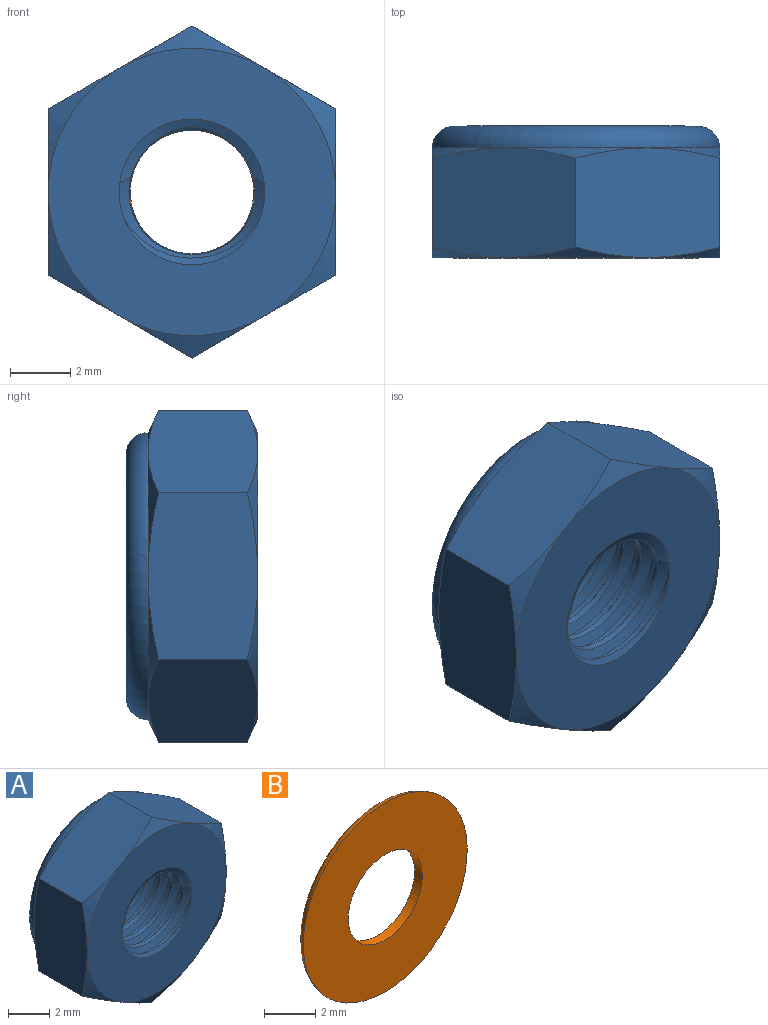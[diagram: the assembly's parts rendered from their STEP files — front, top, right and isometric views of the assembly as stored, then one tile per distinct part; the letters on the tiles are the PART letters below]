
ASSEMBLY  parts=2 mates=1
PART A: 50 faces, bbox 11.4x4.8x11.4 mm
  f0: plane 8.07x8.07mm, normal (0,1,0), area 22.1mm2, adj f1,f49
  f1: torus R=4.03mm, axis (0,-1,0), area 32.3mm2, adj f0,f2,f44,f45,f46,f47,f48
  f2: cone r=4.76mm half-angle=65deg, axis (0,-1,0), area 2.1mm2, adj f1,f3,f43
  f3: plane 5.19x4.07mm, normal (0.5,0,0.87), area 18.7mm2, adj f2,f4,f41,f42,f43,f44
  f4: cone r=5.5mm half-angle=65deg, axis (0,1,0), area 2.1mm2, adj f3,f5,f43
  f5: plane 9.53x9.53mm, normal (0,-1,0), area 53mm2, adj f4,f6,f10,f11,f12,f13,f38,f40
  f6: cone r=5.5mm half-angle=65deg, axis (0,1,0), area 2.1mm2, adj f5,f7,f43
  f7: plane 5.19x4.07mm, normal (0.5,0,-0.87), area 18.7mm2, adj f6,f8,f10,f43,f47,f48
  f8: plane 5.19x4.07mm, normal (-0.5,0,-0.87), area 18.7mm2, adj f7,f9,f10,f11,f46,f47
  f9: plane 5.94x4.07mm, normal (-1,0,0), area 18.7mm2, adj f8,f11,f12,f42,f45,f46
  f10: cone r=5.5mm half-angle=65deg, axis (0,1,0), area 2.1mm2, adj f5,f7,f8
  f11: cone r=5.5mm half-angle=65deg, axis (0,1,0), area 2.1mm2, adj f5,f8,f9
  f12: cone r=5.5mm half-angle=65deg, axis (0,1,0), area 2.1mm2, adj f5,f9,f42
  f13: cone r=2.41mm half-angle=65deg, axis (0,-1,0), area 2.3mm2, adj f5,f14,f15,f16
  f14: cone r=2.09mm half-angle=60deg, axis (0,-0.99,-0.16), area 3.1mm2, adj f13,f15,f40
  f15: cylinder r=2.09mm len=4.18mm, axis (0,0.99,0.16), area 1.8mm2, adj f13,f14,f16
  f16: cone r=2.52mm half-angle=60deg, axis (0,0.99,0.16), area 5.5mm2, adj f13,f15,f17
  f17: cylinder r=2.41mm len=4.83mm, axis (0,-1,0), area 2.9mm2, adj f16,f18
  f18: cone r=2.09mm half-angle=60deg, axis (0,-0.99,-0.16), area 5mm2, adj f17,f19
  f19: cylinder r=2.09mm len=4.18mm, axis (0,0.99,0.16), area 2.6mm2, adj f18,f20
  f20: cone r=2.52mm half-angle=60deg, axis (0,0.99,0.16), area 5.6mm2, adj f19,f21
  f21: cylinder r=2.41mm len=4.83mm, axis (0,-1,0), area 2.9mm2, adj f20,f22
  f22: cone r=2.09mm half-angle=60deg, axis (0,-0.99,-0.16), area 5mm2, adj f21,f23
  f23: cylinder r=2.09mm len=4.18mm, axis (0,0.99,0.16), area 2.6mm2, adj f22,f24
  f24: cone r=2.52mm half-angle=60deg, axis (0,0.99,0.16), area 5.6mm2, adj f23,f25
  f25: cylinder r=2.41mm len=4.83mm, axis (0,-1,0), area 2.9mm2, adj f24,f26
  f26: cone r=2.09mm half-angle=60deg, axis (0,-0.99,-0.16), area 5mm2, adj f25,f27
  f27: cylinder r=2.09mm len=4.18mm, axis (0,0.99,0.16), area 2.6mm2, adj f26,f28
  f28: cone r=2.52mm half-angle=60deg, axis (0,0.99,0.16), area 5.6mm2, adj f27,f29
  f29: cylinder r=2.41mm len=4.83mm, axis (0,-1,0), area 2.9mm2, adj f28,f30
  f30: cone r=2.09mm half-angle=60deg, axis (0,-0.99,-0.16), area 4.2mm2, adj f29,f31,f35
  f31: cylinder r=2.09mm len=4.18mm, axis (0,0.99,0.16), area 1.6mm2, adj f30,f32,f35
  f32: cone r=2.52mm half-angle=60deg, axis (0,0.99,0.16), area 2.7mm2, adj f31,f33,f34,f35
  f33: cylinder r=2.41mm len=1.1mm, axis (0,-1,0), area 0mm2, adj f32,f35
  f34: cone r=2.09mm half-angle=60deg, axis (0,-0.99,-0.16), area 0mm2, adj f32,f35
  f35: plane 9.56x9.56mm, normal (0,1,0), area 50.5mm2, adj f30,f31,f32,f33,f34,f36
  f36: torus R=4.03mm, axis (0,-1,0), area 25mm2, adj f35,f37
  f37: plane 8.07x8.07mm, normal (0,-1,0), area 22.1mm2, adj f36,f49
  f38: cone r=2.41mm half-angle=65deg, axis (0,-1,0), area 0mm2, adj f5,f39
  f39: cone r=2.52mm half-angle=60deg, axis (0,0.99,0.16), area 0mm2, adj f38,f40
  f40: cylinder r=2.41mm len=4.83mm, axis (0,-1,0), area 1.3mm2, adj f5,f14,f39
  f41: cone r=5.5mm half-angle=65deg, axis (0,1,0), area 2.1mm2, adj f3,f5,f42
  f42: plane 5.19x4.07mm, normal (-0.5,0,0.87), area 18.7mm2, adj f3,f9,f12,f41,f44,f45
  f43: plane 5.94x4.07mm, normal (1,0,0), area 18.7mm2, adj f2,f3,f4,f6,f7,f48
  f44: cone r=4.76mm half-angle=65deg, axis (0,-1,0), area 2.1mm2, adj f1,f3,f42
  f45: cone r=4.76mm half-angle=65deg, axis (0,-1,0), area 2.1mm2, adj f1,f9,f42
  f46: cone r=4.76mm half-angle=65deg, axis (0,-1,0), area 2.1mm2, adj f1,f8,f9
  f47: cone r=4.76mm half-angle=65deg, axis (0,-1,0), area 2.1mm2, adj f1,f7,f8
  f48: cone r=4.76mm half-angle=65deg, axis (0,-1,0), area 2.1mm2, adj f1,f7,f43
  f49: cylinder r=3.04mm len=6.08mm, axis (0,-1,0), area 2.9mm2, adj f0,f37
PART B: 4 faces, bbox 9.8x0.5x9.8 mm
  f0: cylinder r=2.05mm len=4.09mm, axis (0,-1,0), area 5.4mm2, adj f1,f3
  f1: plane 9.06x9.06mm, normal (0,-1,0), area 51.3mm2, adj f0,f2
  f2: torus R=4.03mm, axis (0,-1,0), area 19.3mm2, adj f1,f3
  f3: plane 8.07x8.07mm, normal (0,1,0), area 38mm2, adj f0,f2
PLACE A at identity
PLACE B at identity
MATE fastened A.f1 <-> B.f2  axis (0,-1,0) through (0,0,0)mm
